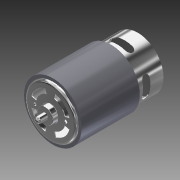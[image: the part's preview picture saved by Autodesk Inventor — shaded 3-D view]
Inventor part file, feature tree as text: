
AUTODESK INVENTOR PART (.ipt)
format: ipt  version: 2014 SP1 (Build 180222100, 222)  size: 371,712 bytes
history: native  units: mm (DEFAULTED — no unit token found)
features: sketch x15, extrude x13, fillet x3, pattern_circular x3, plane x3, hole x2, mirror x2, shell x1, chamfer x1
ambient origin geometry x8: Origin, YZ Plane, XZ Plane, XY Plane, X Axis, Y Axis, Z Axis, Center Point
bodies: Solid1 (feature_tree)
feature tree (43):
  extrude  "Extrusion1"  Depth=71.3mm TaperAngle=0.0deg
  fillet  "Fillet1"  Radius=2.0mm
  shell  "Shell1"  Thickness=0.62mm
  extrude  "Extrusion2"  Depth=4.5mm TaperAngle=0.0deg
  fillet  "Fillet2"  Radius=0.5mm
  extrude  "Extrusion3"  Depth=7.6mm TaperAngle=0.0deg
  fillet  "Fillet3"  Radius=2.5mm
  hole  "Hole1"  [1 undecoded]
  mirror  "Mirror1"
  extrude  "Extrusion4"  Depth=16.0mm
  pattern_circular  "Circular Pattern1"  Count=4 Angle=360.0deg
  plane  "Work Plane1"
  extrude  "Extrusion5"  Depth=0.62mm TaperAngle=0.0deg
  extrude  "Extrusion6"  Depth=0.62mm TaperAngle=0.0deg
  extrude  "Extrusion7"  Depth=3.0mm TaperAngle=0.0deg
  extrude  "Extrusion8"  Depth=0.8mm TaperAngle=0.0deg
  extrude  "Extrusion9"  Depth=1.0mm TaperAngle=0.0deg
  extrude  "Extrusion10"  Depth=3.15mm
  pattern_circular  "Circular Pattern2"  [2 undecoded]
  extrude  "Extrusion11"  Depth=5.9mm TaperAngle=0.0deg
  chamfer  "Chamfer1"  Distance=40.0mm Angle=360.0deg
  hole  "Hole2"  [1 undecoded]
  mirror  "Mirror2"
  plane  "Work Plane2"
  extrude  "Extrusion12"  Depth=5.9mm
  plane  "Work Plane3"
  extrude  "Flux Ring"  Depth=5.9mm
  pattern_circular  "Circular Pattern3"  [2 undecoded]
  sketch  "Sketch1"  dims[d0=42.1mm d1=71.3mm d2=0.0mm d3=2.0mm d4=0.62mm]
  sketch  "Sketch2"  dims[d5=13.0mm d6=4.5mm d7=0.0mm d8=0.5mm]
  sketch  "Sketch3"  dims[d9=5.0mm d10=7.6mm d11=0.0mm d12=2.5mm]
  sketch  "Sketch4"  dims[d13=12.5mm]
  sketch  "Sketch5"  dims[d14=2.5mm d15=6.0mm d16=4.0mm d17=2.0mm d18=14.3117mm d19=8.0mm d20=20.594885mm d21=15.0deg]
  sketch  "Sketch6"  dims[d22=15.0deg d23=16.0mm]
  sketch  "Sketch7"  dims[d24=12.0mm]
  sketch  "Sketch8"  dims[d25=10.0mm d26=0.0mm d27=40.0mm d29=360.0deg]
  sketch  "Sketch9"  dims[d30=-1.75mm d31=0.62mm d32=0.0mm]
  sketch  "Sketch10"  dims[d33=24.0mm d34=0.62mm d35=0.0mm]
  sketch  "Sketch11"  dims[d36=10.75mm d37=3.0mm d38=0.0mm]
  sketch  "Sketch12"  dims[d39=6.9mm d40=0.8mm d41=0.0mm]
  sketch  "Sketch13"  dims[d42=3.2mm d43=1.0mm d44=0.0mm]
  sketch  "Sketch14"  dims[d45=3.15mm d46=3.15mm]
  sketch  "Sketch15"  dims[d47=9.875mm d48=6.5mm d49=1.0mm d50=0.0mm d51=40.0mm d53=360.0deg d54=0.5mm d55=3.8mm d56=14.0mm d57=7.2mm d58=0.0mm d59=1.0mm d60=2.0mm d61=3.0mm d62=2.0mm d63=6.0mm d64=4.0mm d65=2.0mm d66=14.3117mm d67=1.0mm d68=20.594885mm d69=18.0mm d70=10.75mm d71=5.9mm d72=12.0mm d73=7.2mm d74=0.0mm d75=45.0deg d76=2.45mm d77=47.5mm d78=0.0mm d79=40.0mm d80=360.0deg]
note: 6 required parameter values undecoded (feature->parameter linkage not recoverable at this tier; creation-order binding heuristic only, values carry confidence <= 0.55)
